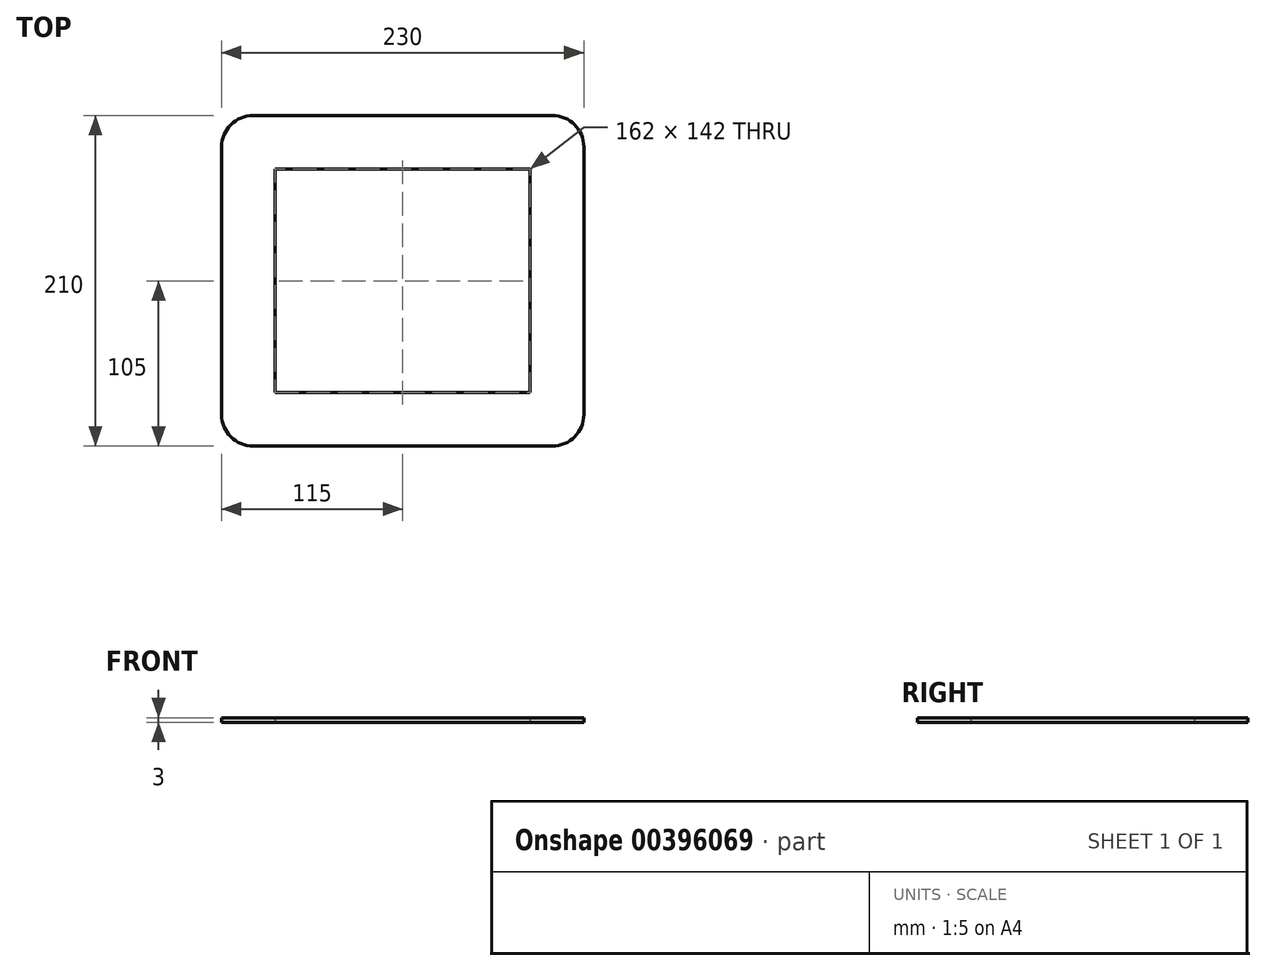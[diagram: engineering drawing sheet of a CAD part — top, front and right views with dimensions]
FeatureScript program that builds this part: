
annotation { "Feature Type Name" : "Feature", "Feature Type Description" : "" }
export const myFeature = defineFeature(function(context is Context, id is Id, definition is map)
    precondition{}
    {
        {
            var Q0;
            Q0=qCreatedBy(makeId("Top.planeOp"),FACE);
            var sketch = newSketch(context, id + "F0", { "sketchPlane" : qUnion([Q0])});
            skLineSegment(sketch, "E0.bottom", {"start": v(-95, 105) * mm, "end": v(95, 105) * mm});
            skLineSegment(sketch, "E0.top", {"start": v(-95, -105) * mm, "end": v(95, -105) * mm});
            skLineSegment(sketch, "E0.left", {"start": v(-115, 85) * mm, "end": v(-115, -85) * mm});
            skLineSegment(sketch, "E0.right", {"start": v(115, 85) * mm, "end": v(115, -85) * mm});
            skPoint(sketch, "E0.middle", {"position": v(0, 0) * mm});
            skPoint(sketch, "E1.visualSharp", {"position": v(-115, 105) * mm});
            skArc(sketch, "E1.filletArc", {"start": v(-95, 105) * mm, "mid": v(-109.14, 99.14) * mm, "end": v(-115, 85) * mm});
            skPoint(sketch, "E2.visualSharp", {"position": v(-115, -105) * mm});
            skArc(sketch, "E2.filletArc", {"start": v(-115, -85) * mm, "mid": v(-109.14, -99.14) * mm, "end": v(-95, -105) * mm});
            skPoint(sketch, "E3.visualSharp", {"position": v(115, -105) * mm});
            skArc(sketch, "E3.filletArc", {"start": v(95, -105) * mm, "mid": v(109.14, -99.14) * mm, "end": v(115, -85) * mm});
            skPoint(sketch, "E4.visualSharp", {"position": v(115, 105) * mm});
            skArc(sketch, "E4.filletArc", {"start": v(115, 85) * mm, "mid": v(109.14, 99.14) * mm, "end": v(95, 105) * mm});
            skLineSegment(sketch, "E5.bottom", {"start": v(-81, 71) * mm, "end": v(81, 71) * mm});
            skLineSegment(sketch, "E5.top", {"start": v(-81, -71) * mm, "end": v(81, -71) * mm});
            skLineSegment(sketch, "E5.left", {"start": v(-81, 71) * mm, "end": v(-81, -71) * mm});
            skLineSegment(sketch, "E5.right", {"start": v(81, 71) * mm, "end": v(81, -71) * mm});
            skSolve(sketch);
        }
        {
            var Q0;
            Q0=qSketchRegion(id+"F0",true);
            extrude(context, id + "F1", {"entities" : qUnion([Q0]), "depth" : 3 * mm});
        }
    });
